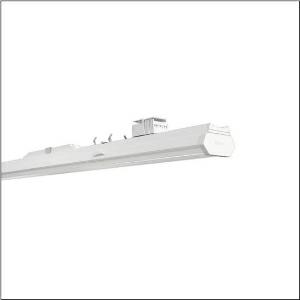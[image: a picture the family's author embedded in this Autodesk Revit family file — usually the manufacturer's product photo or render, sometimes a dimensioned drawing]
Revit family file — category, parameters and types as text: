
# Revit family: licross_r__11_protected_tw_51tp12tnt85x_7ce4
name_source: partatom
category: Lighting Fixtures
units: mm (PartAtom-declared; Revit-internal decimal feet)

## family parameters
Cut with Voids When Loaded = No
Host = Face
Light Source = No
Part Type = Normal
Room Calculation Point = No
Round Connector Dimension = Use Diameter
Shared = No

## types (1)
- --- (1 x LED 2700 K ... 6500 K, 8840 lm, 56 W, 2700K)
    Apparent Load = 56 VA
    CIE Flux Codes = 70 91 97 98 100
    Color Rendering = 80
    Color Temperature = 2700K
    Default Elevation = 1800 mm
    Description = Licross® 11 Protected TW, luminaire insert, of sheet steel, galvanised, coil coated, white, length: 1.500mm, width: 90mm, height: 101mm, LED rated luminous flux: 8.840lm, light colour: 8tw, control gear: DALI DT8, with plug, 5-pole, with phase selection, mains connection: 220..240V, AC, 50/60Hz, rated input power: 56W, halogen-free wiring, primary optical cover: cover, of PMMA, light emission: direct distribution, primary light characteristic: symmetric, protection rating (complete): IP64, insulation class (complete): insulation class I (protective earthing), certification: CE, ENEC, VDE, UKCA, protection symbol: D if used in an environment with conductive dust loads with corresponding accessories, impact resistance: IK06, permissible ambient temperature for indoor applications: -25..+35°C, corresponds to IFS (International Featured Standards) requirements for safety and quality in the food industry, reducing of maximum allowable ambient temperature of 5°C with ceiling mounting, LABS conformity tested according to VDMA 24364:2018-05, packaging unit: 1 piece
    Height = 92 mm
    Lamp = 1 x LED 2700 K ... 6500 K
    Lamp Light Flux = 8840 lm
    Lamp Power = 56 W
    Lamp count = 1
    Length = 1500 mm
    Luminous efficacy = 158 lm/W
    Manufacturer = Siteco
    ModVariant = No
    Model = 51TP12TNT85X
    Mounting Place = Ceiling
    Mounting Type = Pendant
    Number of Poles = 1
    OnlyDefault = Yes
    Power Factor = 1
    Product Name = Licross® 11 Protected TW
    Product group = luminaire insert
    ProductGroupID = 902
    Protection Class = Protection class I
    Protection Degree = IP 64
    RLX_Detail_Level = 1
    RLX_Emergency_Light_Flux = 0 lm
    RLX_Emergency_Type = 0
    RLX_Emergency_Type_DB = No
    RlxData = <blob elided: 20593 chars, md5=d6b85b46>
    Socket = socket
    Standby Power = 0 W
    System Light Flux = 8840 lm
    System Power = 56 W
    Type Comments = individual setting: CCT=2700K
    Type Image = l_1256148.jpg
    URL = http://relux.com
    VarID = @adj_049218
    Voltage = 0 V
    Weight = 0.00 kg
    Width = 88 mm

## geometry (parser evidence)
native form markers: Blend x4, Sweep x11
no freeform markers — native parametric forms only
